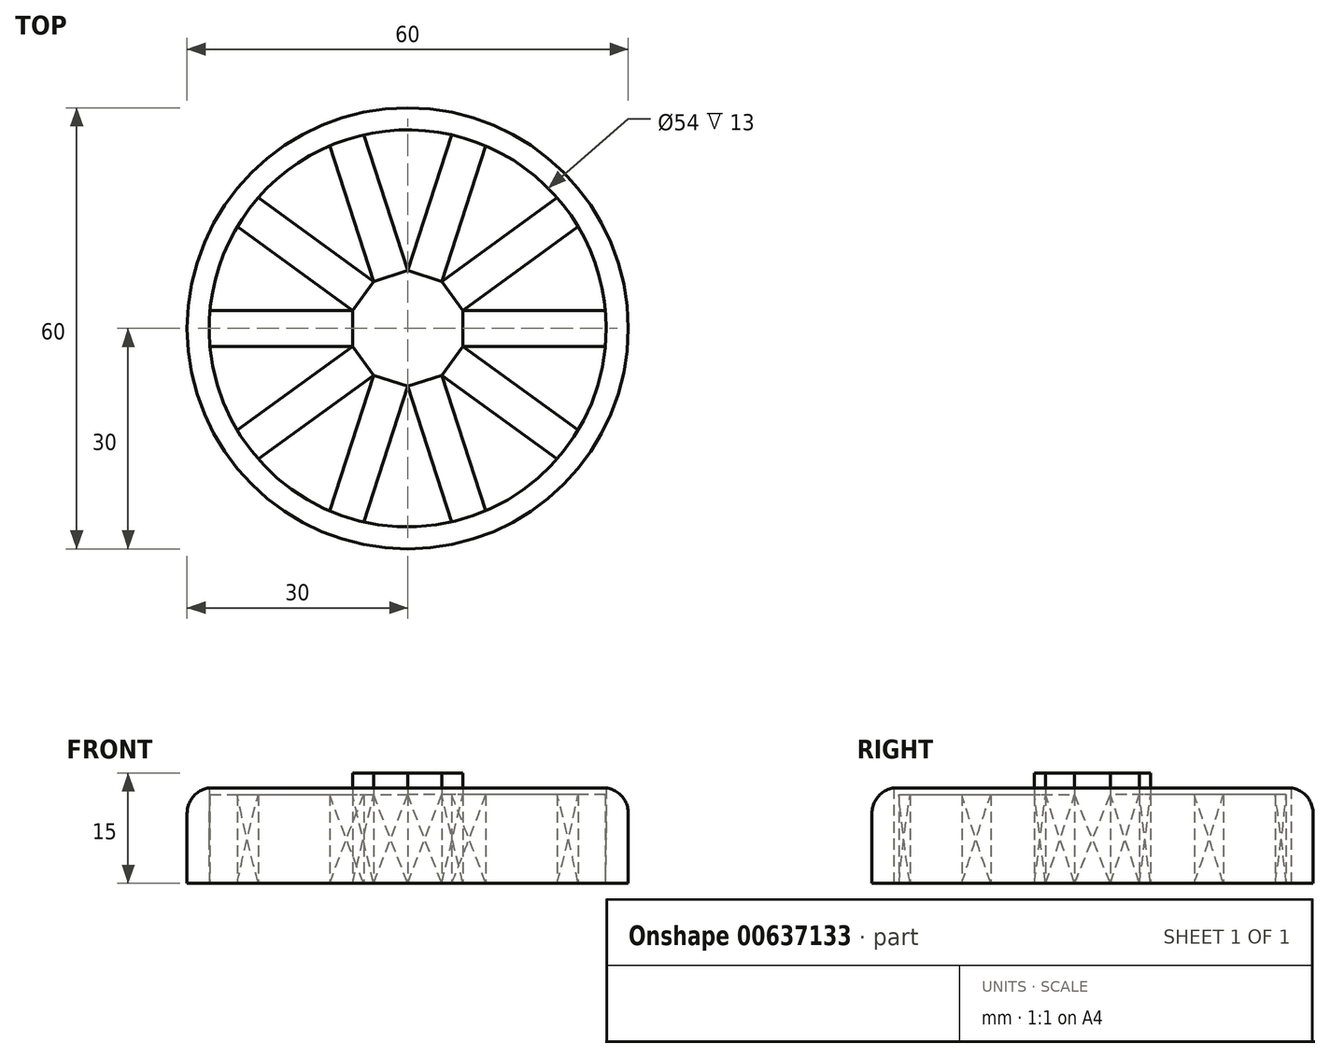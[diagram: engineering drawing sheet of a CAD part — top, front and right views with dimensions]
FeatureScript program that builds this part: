
annotation { "Feature Type Name" : "Feature", "Feature Type Description" : "" }
export const myFeature = defineFeature(function(context is Context, id is Id, definition is map)
    precondition{}
    {
        {
            var Q0;
            Q0=qCreatedBy(makeId("Top.planeOp"),FACE);
            var sketch = newSketch(context, id + "F0", { "sketchPlane" : qUnion([Q0])});
            skCircle(sketch, "E0.cCircle", {"center": v(0, 0) * mm, "radius": 7.5 * mm, "construction": true});
            skLineSegment(sketch, "E0.0", {"start": v(7.5, 2.44) * mm, "end": v(7.5, -2.44) * mm});
            skLineSegment(sketch, "E0.1", {"start": v(7.5, -2.44) * mm, "end": v(4.64, -6.38) * mm});
            skLineSegment(sketch, "E0.2", {"start": v(4.64, -6.38) * mm, "end": v(0, -7.89) * mm});
            skLineSegment(sketch, "E0.3", {"start": v(0, -7.89) * mm, "end": v(-4.64, -6.38) * mm});
            skLineSegment(sketch, "E0.4", {"start": v(-4.64, -6.38) * mm, "end": v(-7.5, -2.44) * mm});
            skLineSegment(sketch, "E0.5", {"start": v(-7.5, -2.44) * mm, "end": v(-7.5, 2.44) * mm});
            skLineSegment(sketch, "E0.6", {"start": v(-7.5, 2.44) * mm, "end": v(-4.64, 6.38) * mm});
            skLineSegment(sketch, "E0.7", {"start": v(-4.64, 6.38) * mm, "end": v(0, 7.89) * mm});
            skLineSegment(sketch, "E0.8", {"start": v(0, 7.89) * mm, "end": v(4.64, 6.38) * mm});
            skLineSegment(sketch, "E0.9", {"start": v(4.64, 6.38) * mm, "end": v(7.5, 2.44) * mm});
            skPoint(sketch, "E0.0.midPoint", {"position": v(7.5, 0) * mm});
            skSolve(sketch);
        }
        {
            var Q0;
            Q0=makeQuery(id+"F0.imprint","IMPRINT",FACE,{"disambiguationData":[TD([[makeQuery(id+"F0.imprint","IMPRINT",EDGE,{"derivedFrom":sQuery(id+"F0.wireOp",EDGE,"E0.0")}),-1.0]])]});
            extrude(context, id + "F1", {"entities" : qUnion([Q0]), "depth" : 15 * mm, "offsetDistance" : 25 * mm});
        }
        {
            var Q0;
            Q0=makeQuery(id+"F1.opExtrude","SWEPT_FACE",FACE,{"disambiguationData":[OSD([sQuery(id+"F0.wireOp",EDGE,"E0.3")])]});
            var sketch = newSketch(context, id + "F2", { "sketchPlane" : qUnion([Q0])});
            skLineSegment(sketch, "E1", {"start": v(-2.44, 0) * mm, "end": v(2.44, 12.05) * mm});
            skLineSegment(sketch, "E2", {"start": v(2.44, 12.05) * mm, "end": v(2.44, 0) * mm});
            skLineSegment(sketch, "E3", {"start": v(2.44, 0) * mm, "end": v(-2.44, 0) * mm});
            skSolve(sketch);
        }
        {
            var Q0;
            Q0=makeQuery(id+"F2.imprint","IMPRINT",FACE,{"disambiguationData":[TD([[makeQuery(id+"F2.imprint","IMPRINT",EDGE,{"derivedFrom":sQuery(id+"F2.wireOp",EDGE,"E1")}),-1.0]])]});
            extrude(context, id + "F3", {"entities" : qUnion([Q0]), "operationType" : NewBodyOperationType.ADD, "depth" : 20 * mm, "offsetDistance" : 25 * mm});
        }
        {
            var Q0;
            Q0=makeQuery(id+"F1.opExtrude","SWEPT_FACE",FACE,{"disambiguationData":[OSD([sQuery(id+"F0.wireOp",EDGE,"E0.4")])]});
            var sketch = newSketch(context, id + "F4", { "sketchPlane" : qUnion([Q0])});
            skLineSegment(sketch, "E4", {"start": v(-2.44, 0) * mm, "end": v(2.44, 12.05) * mm});
            skLineSegment(sketch, "E5", {"start": v(2.44, 12.05) * mm, "end": v(2.44, 0) * mm});
            skLineSegment(sketch, "E6", {"start": v(2.44, 0) * mm, "end": v(-2.44, 0) * mm});
            skSolve(sketch);
        }
        {
            var Q0;
            Q0=makeQuery(id+"F4.imprint","IMPRINT",FACE,{"disambiguationData":[TD([[makeQuery(id+"F4.imprint","IMPRINT",EDGE,{"derivedFrom":sQuery(id+"F4.wireOp",EDGE,"E4")}),-1.0]])]});
            extrude(context, id + "F5", {"entities" : qUnion([Q0]), "operationType" : NewBodyOperationType.ADD, "depth" : 20 * mm, "offsetDistance" : 25 * mm});
        }
        {
            var Q0;
            Q0=makeQuery(id+"F1.opExtrude","SWEPT_FACE",FACE,{"disambiguationData":[OSD([sQuery(id+"F0.wireOp",EDGE,"E0.5")])]});
            var sketch = newSketch(context, id + "F6", { "sketchPlane" : qUnion([Q0])});
            skLineSegment(sketch, "E7", {"start": v(-2.44, 0) * mm, "end": v(2.44, 12.05) * mm});
            skLineSegment(sketch, "E8", {"start": v(2.44, 12.05) * mm, "end": v(2.44, 0) * mm});
            skLineSegment(sketch, "E9", {"start": v(2.44, 0) * mm, "end": v(-2.44, 0) * mm});
            skSolve(sketch);
        }
        {
            var Q0;
            Q0=makeQuery(id+"F1.opExtrude","SWEPT_FACE",FACE,{"disambiguationData":[OSD([sQuery(id+"F0.wireOp",EDGE,"E0.6")])]});
            var sketch = newSketch(context, id + "F7", { "sketchPlane" : qUnion([Q0])});
            skLineSegment(sketch, "E10", {"start": v(-2.44, 0) * mm, "end": v(2.44, 12.05) * mm});
            skLineSegment(sketch, "E11", {"start": v(2.44, 12.05) * mm, "end": v(2.44, 0) * mm});
            skLineSegment(sketch, "E12", {"start": v(2.44, 0) * mm, "end": v(-2.44, 0) * mm});
            skSolve(sketch);
        }
        {
            var Q0;
            Q0=makeQuery(id+"F1.opExtrude","SWEPT_FACE",FACE,{"disambiguationData":[OSD([sQuery(id+"F0.wireOp",EDGE,"E0.7")])]});
            var sketch = newSketch(context, id + "F8", { "sketchPlane" : qUnion([Q0])});
            skLineSegment(sketch, "E13", {"start": v(-2.44, 0) * mm, "end": v(2.44, 12.05) * mm});
            skLineSegment(sketch, "E14", {"start": v(2.44, 12.05) * mm, "end": v(2.44, 0) * mm});
            skLineSegment(sketch, "E15", {"start": v(2.44, 0) * mm, "end": v(-2.44, 0) * mm});
            skSolve(sketch);
        }
        {
            var Q0;
            Q0=makeQuery(id+"F1.opExtrude","SWEPT_FACE",FACE,{"disambiguationData":[OSD([sQuery(id+"F0.wireOp",EDGE,"E0.8")])]});
            var sketch = newSketch(context, id + "F9", { "sketchPlane" : qUnion([Q0])});
            skLineSegment(sketch, "E16", {"start": v(-2.44, 0) * mm, "end": v(2.44, 12.05) * mm});
            skLineSegment(sketch, "E17", {"start": v(2.44, 12.05) * mm, "end": v(2.44, 0) * mm});
            skLineSegment(sketch, "E18", {"start": v(2.44, 0) * mm, "end": v(-2.44, 0) * mm});
            skSolve(sketch);
        }
        {
            var Q0;
            Q0=makeQuery(id+"F1.opExtrude","SWEPT_FACE",FACE,{"disambiguationData":[OSD([sQuery(id+"F0.wireOp",EDGE,"E0.9")])]});
            var sketch = newSketch(context, id + "F10", { "sketchPlane" : qUnion([Q0])});
            skLineSegment(sketch, "E19", {"start": v(-2.44, 0) * mm, "end": v(2.44, 12.05) * mm});
            skLineSegment(sketch, "E20", {"start": v(2.44, 12.05) * mm, "end": v(2.44, 0) * mm});
            skLineSegment(sketch, "E21", {"start": v(2.44, 0) * mm, "end": v(-2.44, 0) * mm});
            skSolve(sketch);
        }
        {
            var Q0;
            Q0=makeQuery(id+"F1.opExtrude","SWEPT_FACE",FACE,{"disambiguationData":[OSD([sQuery(id+"F0.wireOp",EDGE,"E0.0")])]});
            var sketch = newSketch(context, id + "F11", { "sketchPlane" : qUnion([Q0])});
            skLineSegment(sketch, "E22", {"start": v(-2.44, 0) * mm, "end": v(2.44, 12.05) * mm});
            skLineSegment(sketch, "E23", {"start": v(2.44, 12.05) * mm, "end": v(2.44, 0) * mm});
            skLineSegment(sketch, "E24", {"start": v(2.44, 0) * mm, "end": v(-2.44, 0) * mm});
            skSolve(sketch);
        }
        {
            var Q0;
            Q0=makeQuery(id+"F1.opExtrude","SWEPT_FACE",FACE,{"disambiguationData":[OSD([sQuery(id+"F0.wireOp",EDGE,"E0.1")])]});
            var sketch = newSketch(context, id + "F12", { "sketchPlane" : qUnion([Q0])});
            skLineSegment(sketch, "E25", {"start": v(-2.44, 0) * mm, "end": v(2.44, 12.05) * mm});
            skLineSegment(sketch, "E26", {"start": v(2.44, 12.05) * mm, "end": v(2.44, 0) * mm});
            skLineSegment(sketch, "E27", {"start": v(2.44, 0) * mm, "end": v(-2.44, 0) * mm});
            skSolve(sketch);
        }
        {
            var Q0;
            Q0=makeQuery(id+"F1.opExtrude","SWEPT_FACE",FACE,{"disambiguationData":[OSD([sQuery(id+"F0.wireOp",EDGE,"E0.2")])]});
            var sketch = newSketch(context, id + "F13", { "sketchPlane" : qUnion([Q0])});
            skLineSegment(sketch, "E28", {"start": v(-2.44, 0) * mm, "end": v(2.44, 12.05) * mm});
            skLineSegment(sketch, "E29", {"start": v(2.44, 12.05) * mm, "end": v(2.44, 0) * mm});
            skLineSegment(sketch, "E30", {"start": v(2.44, 0) * mm, "end": v(-2.44, 0) * mm});
            skSolve(sketch);
        }
        {
            var Q0;
            Q0=makeQuery(id+"F13.imprint","IMPRINT",FACE,{"disambiguationData":[TD([[makeQuery(id+"F13.imprint","IMPRINT",EDGE,{"derivedFrom":sQuery(id+"F13.wireOp",EDGE,"E28")}),-1.0]])]});
            extrude(context, id + "F14", {"entities" : qUnion([Q0]), "operationType" : NewBodyOperationType.ADD, "depth" : 20 * mm, "offsetDistance" : 25 * mm});
        }
        {
            var Q0;
            Q0=makeQuery(id+"F12.imprint","IMPRINT",FACE,{"disambiguationData":[TD([[makeQuery(id+"F12.imprint","IMPRINT",EDGE,{"derivedFrom":sQuery(id+"F12.wireOp",EDGE,"E25")}),-1.0]])]});
            extrude(context, id + "F15", {"entities" : qUnion([Q0]), "operationType" : NewBodyOperationType.ADD, "depth" : 20 * mm, "offsetDistance" : 25 * mm});
        }
        {
            var Q0;
            Q0=makeQuery(id+"F11.imprint","IMPRINT",FACE,{"disambiguationData":[TD([[makeQuery(id+"F11.imprint","IMPRINT",EDGE,{"derivedFrom":sQuery(id+"F11.wireOp",EDGE,"E22")}),-1.0]])]});
            extrude(context, id + "F16", {"entities" : qUnion([Q0]), "operationType" : NewBodyOperationType.ADD, "depth" : 20 * mm, "offsetDistance" : 25 * mm});
        }
        {
            var Q0;
            Q0=makeQuery(id+"F10.imprint","IMPRINT",FACE,{"disambiguationData":[TD([[makeQuery(id+"F10.imprint","IMPRINT",EDGE,{"derivedFrom":sQuery(id+"F10.wireOp",EDGE,"E19")}),-1.0]])]});
            extrude(context, id + "F17", {"entities" : qUnion([Q0]), "operationType" : NewBodyOperationType.ADD, "depth" : 20 * mm, "offsetDistance" : 25 * mm});
        }
        {
            var Q0;
            Q0=makeQuery(id+"F9.imprint","IMPRINT",FACE,{"disambiguationData":[TD([[makeQuery(id+"F9.imprint","IMPRINT",EDGE,{"derivedFrom":sQuery(id+"F9.wireOp",EDGE,"E16")}),-1.0]])]});
            extrude(context, id + "F18", {"entities" : qUnion([Q0]), "operationType" : NewBodyOperationType.ADD, "depth" : 20 * mm, "offsetDistance" : 25 * mm});
        }
        {
            var Q0;
            Q0=makeQuery(id+"F8.imprint","IMPRINT",FACE,{"disambiguationData":[TD([[makeQuery(id+"F8.imprint","IMPRINT",EDGE,{"derivedFrom":sQuery(id+"F8.wireOp",EDGE,"E13")}),-1.0]])]});
            extrude(context, id + "F19", {"entities" : qUnion([Q0]), "operationType" : NewBodyOperationType.ADD, "depth" : 20 * mm, "offsetDistance" : 25 * mm});
        }
        {
            var Q0;
            Q0=makeQuery(id+"F7.imprint","IMPRINT",FACE,{"disambiguationData":[TD([[makeQuery(id+"F7.imprint","IMPRINT",EDGE,{"derivedFrom":sQuery(id+"F7.wireOp",EDGE,"E10")}),-1.0]])]});
            extrude(context, id + "F20", {"entities" : qUnion([Q0]), "operationType" : NewBodyOperationType.ADD, "depth" : 20 * mm, "offsetDistance" : 25 * mm});
        }
        {
            var Q0;
            Q0=makeQuery(id+"F6.imprint","IMPRINT",FACE,{"disambiguationData":[TD([[makeQuery(id+"F6.imprint","IMPRINT",EDGE,{"derivedFrom":sQuery(id+"F6.wireOp",EDGE,"E7")}),-1.0]])]});
            extrude(context, id + "F21", {"entities" : qUnion([Q0]), "operationType" : NewBodyOperationType.ADD, "depth" : 20 * mm, "offsetDistance" : 25 * mm});
        }
        {
            var Q0;
            Q0=qCreatedBy(makeId("Top.planeOp"),FACE);
            var sketch = newSketch(context, id + "F22", { "sketchPlane" : qUnion([Q0])});
            skCircle(sketch, "E31", {"center": v(0, 0) * mm, "radius": 30 * mm});
            skSolve(sketch);
        }
        {
            var Q0;
            Q0=makeQuery(id+"F22.imprint","IMPRINT",FACE,{"disambiguationData":[TD([[makeQuery(id+"F22.imprint","IMPRINT",EDGE,{"derivedFrom":sQuery(id+"F22.wireOp",EDGE,"E31")}),1.0]])]});
            var sketch = newSketch(context, id + "F23", { "sketchPlane" : qUnion([Q0])});
            skCircle(sketch, "E32", {"center": v(0, 0) * mm, "radius": 27 * mm});
            skSolve(sketch);
        }
        {
            var Q0;
            Q0=makeQuery(id+"F23.imprint","IMPRINT",FACE,{"disambiguationData":[TD([[makeQuery(id+"F23.imprint","IMPRINT",EDGE,{"derivedFrom":sQuery(id+"F23.wireOp",EDGE,"E32")}),-1.0]])]});
            extrude(context, id + "F24", {"entities" : qUnion([Q0]), "operationType" : NewBodyOperationType.ADD, "depth" : 13 * mm, "offsetDistance" : 25 * mm});
        }
        {
            var Q0;
            Q0=makeQuery(id+"F24.opExtrude","CAP_EDGE",EDGE,{"disambiguationData":[OSD([sQuery(id+"F22.wireOp",EDGE,"E31")])],"isStart":false});
            fillet(context, id + "F25", {"entities" : qUnion([Q0]), "radius" : 3.5 * mm, "tangentPropagation" : true, "allowEdgeOverflow" : false});
        }
        {
            var Q0;
            Q0=makeQuery(id+"F22.imprint","IMPRINT",FACE,{"disambiguationData":[TD([[makeQuery(id+"F22.imprint","IMPRINT",EDGE,{"derivedFrom":sQuery(id+"F22.wireOp",EDGE,"E31")}),1.0]])]});
            var sketch = newSketch(context, id + "F26", { "sketchPlane" : qUnion([Q0])});
            skCircle(sketch, "E33", {"center": v(0, 0) * mm, "radius": 1 * mm});
            skSolve(sketch);
        }
        {
            var Q0;
            Q0=makeQuery(id+"F26.imprint","IMPRINT",FACE,{"disambiguationData":[TD([[makeQuery(id+"F26.imprint","IMPRINT",EDGE,{"derivedFrom":sQuery(id+"F26.wireOp",EDGE,"E33")}),1.0]])]});
            extrude(context, id + "F27", {"entities" : qUnion([Q0]), "operationType" : NewBodyOperationType.ADD, "depth" : 8 * mm, "offsetDistance" : 25 * mm});
        }
    });
